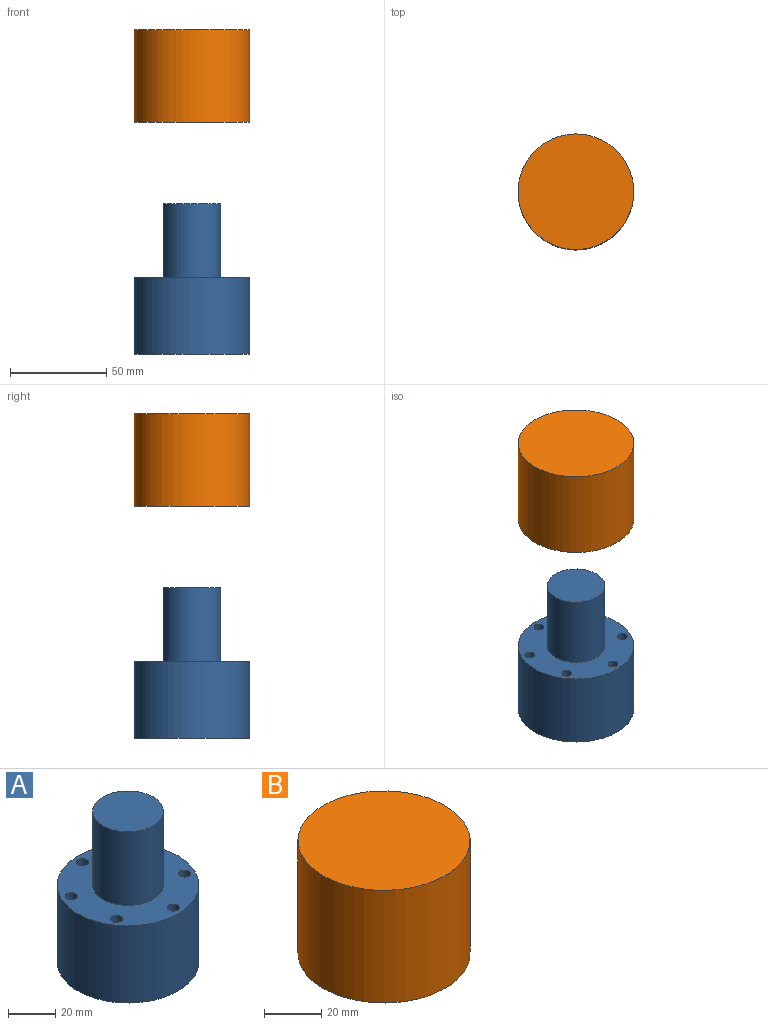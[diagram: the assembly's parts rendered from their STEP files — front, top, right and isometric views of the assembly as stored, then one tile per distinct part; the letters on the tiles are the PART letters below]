
ASSEMBLY  parts=2 mates=1
PART A: 11 faces, bbox 60x60x78.1 mm
  f0: cylinder r=30mm len=60mm, axis (0,0,-1), area 7539.8mm2, adj f1,f2
  f1: plane 60x60mm, normal (0,0,1), area 1999mm2, adj f0,f3,f5,f6,f7,f8,f9,f10
  f2: plane 60x60mm, normal (0,0,-1), area 2705.8mm2, adj f0,f5,f6,f7,f8,f9,f10
  f3: cylinder r=15mm len=38.1mm, axis (0,0,-1), area 3590.8mm2, adj f1,f4
  f4: plane 30x30mm, normal (0,0,1), area 706.9mm2, adj f3
  f5: cylinder r=2.54mm len=40mm, axis (0,0,1), area 638.4mm2, adj f1,f2
  f6: cylinder r=2.54mm len=40mm, axis (0,0,1), area 638.4mm2, adj f1,f2
  f7: cylinder r=2.54mm len=40mm, axis (0,0,1), area 638.4mm2, adj f1,f2
  f8: cylinder r=2.54mm len=40mm, axis (0,0,1), area 638.4mm2, adj f1,f2
  f9: cylinder r=2.54mm len=40mm, axis (0,0,1), area 638.4mm2, adj f1,f2
  f10: cylinder r=2.54mm len=40mm, axis (0,0,1), area 638.4mm2, adj f1,f2
PART B: 5 faces, bbox 60x60x48.1 mm
  f0: cylinder r=15mm len=38.1mm, axis (0,0,-1), area 3590.8mm2, adj f2,f3
  f1: cylinder r=30mm len=60mm, axis (0,0,-1), area 9066.6mm2, adj f2,f4
  f2: plane 60x60mm, normal (0,0,-1), area 2120.6mm2, adj f0,f1
  f3: plane 30x30mm, normal (0,0,-1), area 706.9mm2, adj f0
  f4: plane 60x60mm, normal (0,0,1), area 2827.4mm2, adj f1
PLACE A t=(-12.16,-19.11,-24.59)mm
PLACE B t=(-12.16,-19.11,95.83)mm
MATE cylindrical B.f0 <-> A.f3  axis (0,0,-1) through (-12.16,-19.11,95.83)mm
